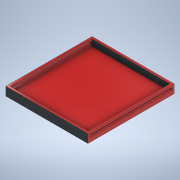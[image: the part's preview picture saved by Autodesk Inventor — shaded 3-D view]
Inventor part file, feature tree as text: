
AUTODESK INVENTOR PART (.ipt)
format: ipt  version: 2020 (Build 240168000, 168)  size: 173,056 bytes
history: native  units: in
note: dims shown in document units (in); Inventor stores cm internally (conversion verified against a paired STEP export)
features: extrude x7, sketch x7, plane x3
ambient origin geometry x8: Origin, YZ Plane, XZ Plane, XY Plane, X Axis, Y Axis, Z Axis, Center Point
bodies: Solid1 (feature_tree)
feature tree (17):
  extrude  "Extrusion1"  Depth=39.3701in
  extrude  "Extrusion2"  Depth=3.1496in
  extrude  "Extrusion3"  Depth=1.0in TaperAngle=0.0deg
  extrude  "Extrusion4"  Depth=3.1496in
  extrude  "Extrusion5"  Depth=39.3701in
  plane  "Work Plane1"
  extrude  "Extrusion6"  Depth=1.0in TaperAngle=0.0deg
  extrude  "Extrusion7"  Depth=1.1811in
  plane  "Work Plane2"
  plane  "Work Plane3"
  sketch  "Sketch1"  dims[d0=39.3701in d1=39.3701in]
  sketch  "Sketch2"  dims[d2=1.0in d3=0.0in d4=3.1496in]
  sketch  "Sketch3"  dims[d5=39.3701in d6=1.0in d7=0.0in]
  sketch  "Sketch4"  dims[d8=39.3701in d9=3.1496in]
  sketch  "Sketch5"  dims[d10=1.0in d11=0.0in d12=39.3701in]
  sketch  "Sketch6"  dims[d13=1.1811in d14=1.0in d15=0.0in]
  sketch  "Sketch7"  dims[d16=39.3701in d17=1.1811in d18=0.9843in d19=1.0in d20=0.0in d21=1.0in d22=0.0in d23=1.0in d24=0.0in d25=0.0in]
